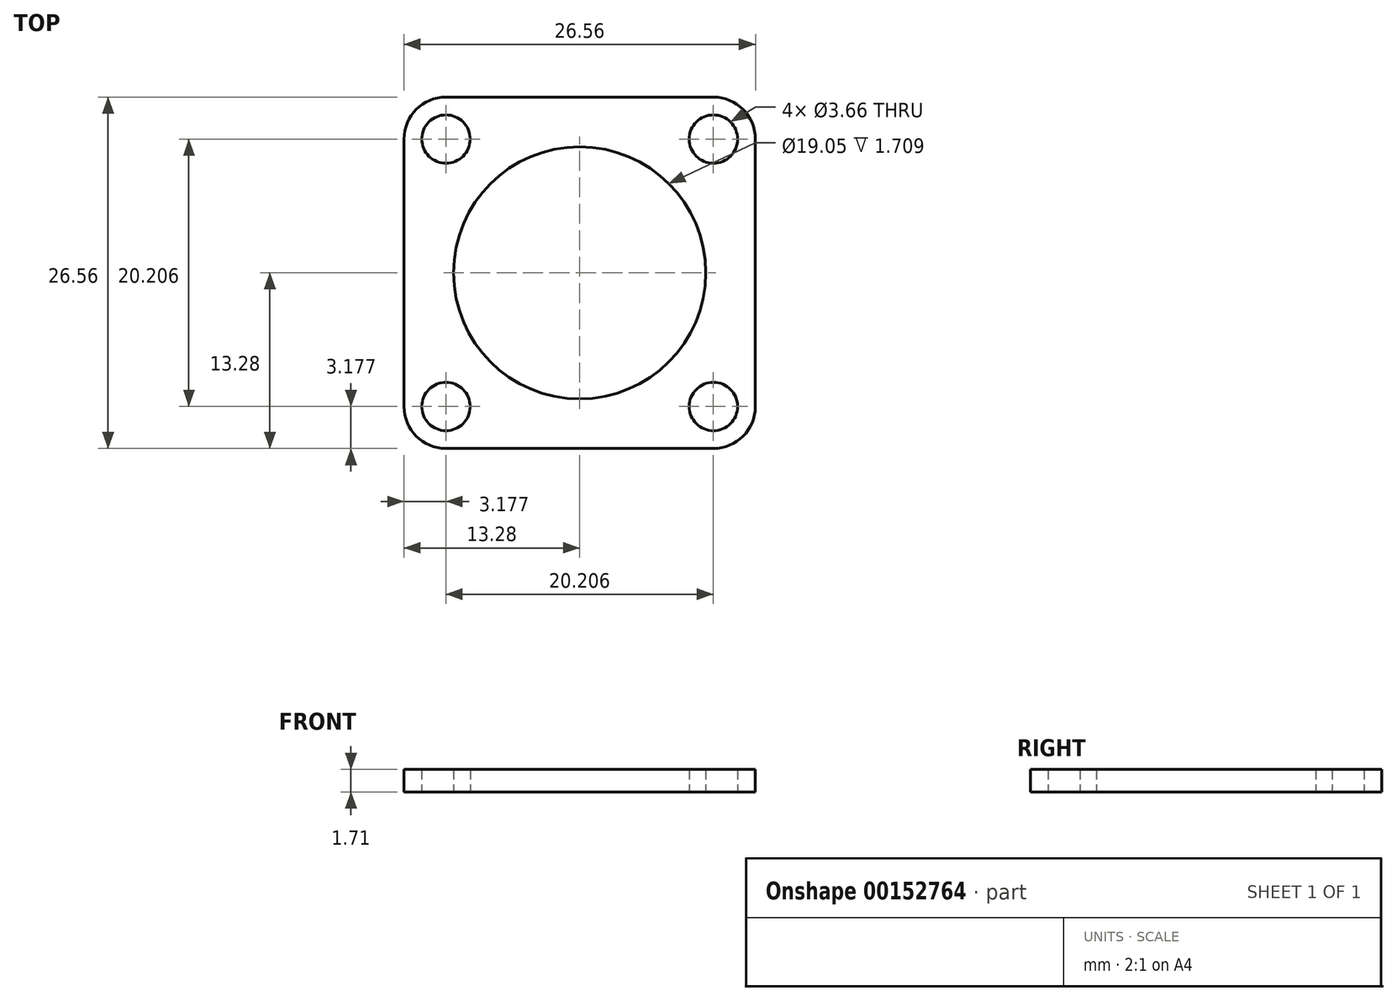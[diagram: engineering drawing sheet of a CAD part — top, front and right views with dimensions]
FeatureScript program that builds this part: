
annotation { "Feature Type Name" : "Feature", "Feature Type Description" : "" }
export const myFeature = defineFeature(function(context is Context, id is Id, definition is map)
    precondition{}
    {
        {
            var Q0;
            Q0=qCreatedBy(makeId("Top.planeOp"),FACE);
            var sketch = newSketch(context, id + "F0", { "sketchPlane" : qUnion([Q0])});
            skLineSegment(sketch, "E0.bottom", {"start": v(13.28, -13.28) * mm, "end": v(-13.28, -13.28) * mm});
            skLineSegment(sketch, "E0.top", {"start": v(13.28, 13.28) * mm, "end": v(-13.28, 13.28) * mm});
            skLineSegment(sketch, "E0.left", {"start": v(13.28, -13.28) * mm, "end": v(13.28, 13.28) * mm});
            skLineSegment(sketch, "E0.right", {"start": v(-13.28, -13.28) * mm, "end": v(-13.28, 13.28) * mm});
            skPoint(sketch, "E0.middle", {"position": v(0, 0) * mm});
            skLineSegment(sketch, "E1.bottom", {"start": v(10.1, -10.1) * mm, "end": v(-10.1, -10.1) * mm, "construction": true});
            skLineSegment(sketch, "E1.top", {"start": v(10.1, 10.1) * mm, "end": v(-10.1, 10.1) * mm, "construction": true});
            skLineSegment(sketch, "E1.left", {"start": v(10.1, -10.1) * mm, "end": v(10.1, 10.1) * mm, "construction": true});
            skLineSegment(sketch, "E1.right", {"start": v(-10.1, -10.1) * mm, "end": v(-10.1, 10.1) * mm, "construction": true});
            skCircle(sketch, "E2", {"center": v(0, 0) * mm, "radius": 11.11 * mm, "construction": true});
            skCircle(sketch, "E3", {"center": v(10.1, -10.1) * mm, "radius": 3.18 * mm, "construction": true});
            skCircle(sketch, "E4", {"center": v(-10.1, 10.1) * mm, "radius": 1.83 * mm});
            skCircle(sketch, "E5", {"center": v(0, 0) * mm, "radius": 9.53 * mm});
            skCircle(sketch, "E6", {"center": v(10.1, 10.1) * mm, "radius": 1.83 * mm});
            skCircle(sketch, "E7", {"center": v(10.1, -10.1) * mm, "radius": 1.83 * mm});
            skCircle(sketch, "E8", {"center": v(-10.1, -10.1) * mm, "radius": 1.83 * mm});
            skSolve(sketch);
        }
        {
            var Q0;
            Q0 = qSketchRegion(id + "F0", true);
            extrude(context, id + "F1", {"entities" : qUnion([Q0]), "depth" : 1.7 * mm});
        }
        {
            var Q0;
            Q0=makeQuery(id+"F1.opExtrude","SWEPT_EDGE",EDGE,{"disambiguationData":[OSD([sQuery(id+"F0.wireOp",EDGE,"E0.top"),sQuery(id+"F0.wireOp",EDGE,"E0.right")])]});
            var Q1;
            Q1=makeQuery(id+"F1.opExtrude","SWEPT_EDGE",EDGE,{"disambiguationData":[OSD([sQuery(id+"F0.wireOp",EDGE,"E0.top"),sQuery(id+"F0.wireOp",EDGE,"E0.left")])]});
            var Q2;
            Q2=makeQuery(id+"F1.opExtrude","SWEPT_EDGE",EDGE,{"disambiguationData":[OSD([sQuery(id+"F0.wireOp",EDGE,"E0.bottom"),sQuery(id+"F0.wireOp",EDGE,"E0.left")])]});
            var Q3;
            Q3=makeQuery(id+"F1.opExtrude","SWEPT_EDGE",EDGE,{"disambiguationData":[OSD([sQuery(id+"F0.wireOp",EDGE,"E0.bottom"),sQuery(id+"F0.wireOp",EDGE,"E0.right")])]});
            fillet(context, id + "F2", {"entities" : qUnion([Q0, Q1, Q2, Q3]), "radius" : 3.17 * mm, "tangentPropagation" : true, "allowEdgeOverflow" : false});
        }
    });
